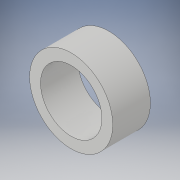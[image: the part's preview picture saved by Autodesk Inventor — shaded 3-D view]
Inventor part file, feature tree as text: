
AUTODESK INVENTOR PART (.ipt)
format: ipt  version: 2019 (Build 230136000, 136)  size: 102,400 bytes
history: native  units: mm
features: extrude x2, sketch x2
ambient origin geometry x8: Origin, YZ Plane, XZ Plane, XY Plane, X Axis, Y Axis, Z Axis, Center Point
bodies: Solid1 (feature_tree)
feature tree (4):
  extrude  "Extrusion1"  Depth=9.5mm TaperAngle=0.0deg
  extrude  "Extrusion2"  Depth=9.5mm TaperAngle=0.0deg
  sketch  "Sketch1"  dims[d0=21.0mm d1=9.5mm d2=0.0mm]
  sketch  "Sketch2"  dims[d3=15.5mm d4=9.5mm d5=0.0mm]
